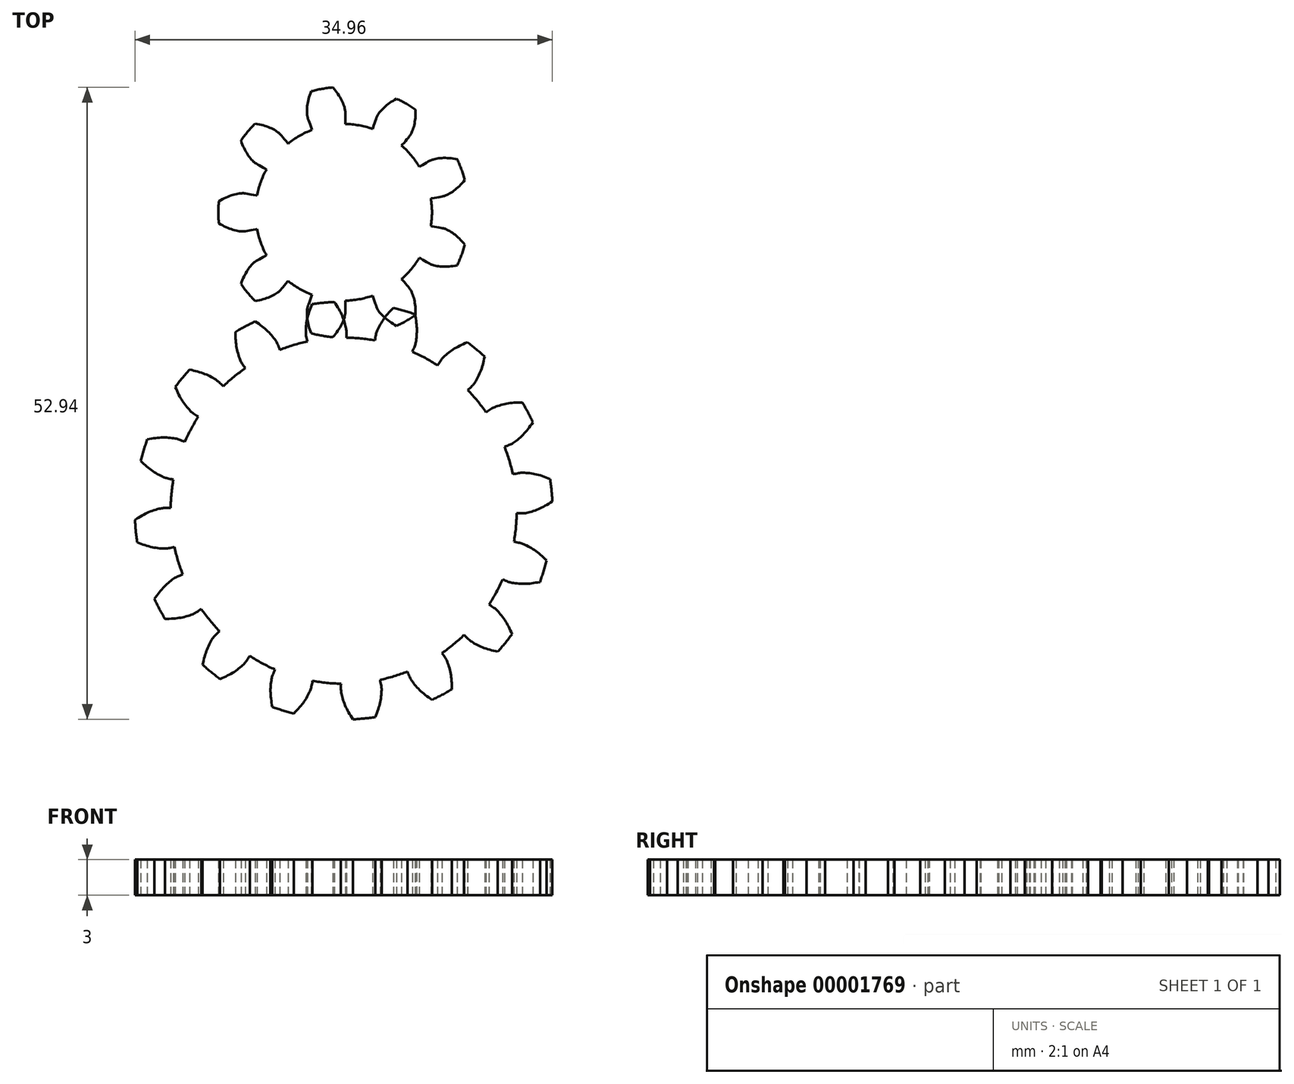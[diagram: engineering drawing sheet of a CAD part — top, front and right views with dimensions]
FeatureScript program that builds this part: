
annotation { "Feature Type Name" : "Feature", "Feature Type Description" : "" }
export const myFeature = defineFeature(function(context is Context, id is Id, definition is map)
    precondition{}
    {
        {
            var Q0;
            Q0=qCreatedBy(makeId("Top.planeOp"),FACE);
            var sketch = newSketch(context, id + "F0", { "sketchPlane" : qUnion([Q0])});
            skCircle(sketch, "E0", {"center": v(0, 0) * mm, "radius": 16 * mm});
            skLineSegment(sketch, "E1", {"start": v(0, 0) * mm, "end": v(0, 25) * mm, "construction": true});
            skLineSegment(sketch, "E2", {"start": v(0, 16) * mm, "end": v(15.76, 16) * mm, "construction": true});
            skLineSegment(sketch, "E3", {"start": v(-5.14, 14.13) * mm, "end": v(0, 16) * mm, "construction": true});
            skCircle(sketch, "E4", {"center": v(0, 0) * mm, "radius": 15.04 * mm});
            skArc(sketch, "E5", {"start": v(0.22, 15.03) * mm, "mid": v(-2.5, 14.83) * mm, "end": v(-5.14, 14.13) * mm, "construction": true});
            skArc(sketch, "E6", {"start": v(-5.14, 14.13) * mm, "mid": v(-6.07, 13.76) * mm, "end": v(-6.97, 13.32) * mm});
            skLineSegment(sketch, "E7", {"start": v(-6.97, 13.32) * mm, "end": v(-0.35, 16.79) * mm});
            skCircle(sketch, "E8", {"center": v(0, 25) * mm, "radius": 9 * mm});
            skCircle(sketch, "E9", {"center": v(0, 25) * mm, "radius": 8.46 * mm});
            skArc(sketch, "E10", {"start": v(-2.73, 14.78) * mm, "mid": v(-3.95, 14.5) * mm, "end": v(-5.14, 14.13) * mm});
            skLineSegment(sketch, "E11", {"start": v(-2.73, 14.78) * mm, "end": v(0.19, 15.32) * mm});
            skCircle(sketch, "E12", {"center": v(0, 0) * mm, "radius": 17.5 * mm});
            skLineSegment(sketch, "E13", {"start": v(0, 0) * mm, "end": v(-2.68, 27.22) * mm, "construction": true});
            skArc(sketch, "E14", {"start": v(-6.97, 13.32) * mm, "mid": v(-7.84, 12.83) * mm, "end": v(-8.68, 12.28) * mm});
            skLineSegment(sketch, "E15", {"start": v(-8.68, 12.28) * mm, "end": v(-0.94, 17.75) * mm});
            skLineSegment(sketch, "E16", {"start": v(0, 34) * mm, "end": v(7.65, 34) * mm, "construction": true});
            skLineSegment(sketch, "E17", {"start": v(0, 34) * mm, "end": v(-2.9, 32.95) * mm});
            skArc(sketch, "E18", {"start": v(0.13, 33.46) * mm, "mid": v(-1.4, 33.34) * mm, "end": v(-2.9, 32.95) * mm});
            skArc(sketch, "E19", {"start": v(-2.9, 32.95) * mm, "mid": v(-3.59, 32.66) * mm, "end": v(-4.25, 32.31) * mm});
            skArc(sketch, "E20", {"start": v(-4.25, 32.31) * mm, "mid": v(-4.88, 31.9) * mm, "end": v(-5.47, 31.45) * mm});
            skArc(sketch, "E21", {"start": v(-1.45, 33.33) * mm, "mid": v(-2.18, 33.17) * mm, "end": v(-2.9, 32.95) * mm});
            skLineSegment(sketch, "E22", {"start": v(-1.45, 33.33) * mm, "end": v(0.1, 33.6) * mm});
            skLineSegment(sketch, "E23", {"start": v(-4.25, 32.31) * mm, "end": v(-0.3, 34.61) * mm});
            skLineSegment(sketch, "E24", {"start": v(-5.47, 31.45) * mm, "end": v(-0.84, 35.38) * mm});
            skCircle(sketch, "E25", {"center": v(0, 25) * mm, "radius": 10.5 * mm});
            skCircle(sketch, "E26", {"center": v(0, 0) * mm, "radius": 14.5 * mm});
            skCircle(sketch, "E27", {"center": v(0, 25) * mm, "radius": 7.5 * mm});
            skLineSegment(sketch, "E28", {"start": v(0.22, 15.03) * mm, "end": v(0.22, 14.5) * mm});
            skLineSegment(sketch, "E29", {"start": v(0.13, 33.46) * mm, "end": v(0.13, 32.5) * mm});
            skArc(sketch, "E30", {"start": v(-5.47, 31.45) * mm, "mid": v(-6.02, 30.94) * mm, "end": v(-6.52, 30.38) * mm});
            skLineSegment(sketch, "E31", {"start": v(-6.52, 30.38) * mm, "end": v(-1.7, 36.23) * mm});
            skLineSegment(sketch, "E32", {"start": v(0, 40.35) * mm, "end": v(0, 25) * mm, "construction": true});
            skLineSegment(sketch, "E33", {"start": v(0, 25) * mm, "end": v(-3.05, 42.28) * mm, "construction": true});
            skSolve(sketch);
        }
        {
            var Q0;
            Q0=qCreatedBy(makeId("Top.planeOp"),FACE);
            var sketch = newSketch(context, id + "F1", { "sketchPlane" : qUnion([Q0])});
            skPoint(sketch, "E34.0", {"position": v(-1.7, 36.23) * mm});
            skLineSegment(sketch, "E34.1", {"start": v(0, 25) * mm, "end": v(-3.05, 42.28) * mm, "construction": true});
            skPoint(sketch, "E34.2", {"position": v(-0.84, 35.38) * mm});
            skPoint(sketch, "E34.3", {"position": v(-0.3, 34.61) * mm});
            skPoint(sketch, "E34.4", {"position": v(0, 34) * mm});
            skPoint(sketch, "E34.5", {"position": v(0.13, 33.46) * mm});
            skPoint(sketch, "E34.6", {"position": v(0.13, 32.5) * mm});
            skLineSegment(sketch, "E34.7", {"start": v(0, 40.35) * mm, "end": v(0, 25) * mm, "construction": true});
            skPoint(sketch, "E34.8", {"position": v(0.1, 33.6) * mm});
            skCircle(sketch, "E34.9", {"center": v(0, 25) * mm, "radius": 7.5 * mm, "construction": true});
            skFitSpline(sketch, "E35", {"points": [v(-1.7, 36.23) * mm, v(-0.84, 35.38) * mm, v(-0.3, 34.61) * mm, v(0, 34) * mm, v(0.1, 33.6) * mm, v(0.13, 33.46) * mm, v(0.13, 32.5) * mm], "startDerivative": vector(4.1, -3.72) * mm, "endDerivative": vector(-0.04, -5.95) * mm});
            skArc(sketch, "E36", {"start": v(-2.72, 35.14) * mm, "mid": v(1.82, 14.66) * mm, "end": v(-0.9, 35.46) * mm, "construction": true});
            skArc(sketch, "E37", {"start": v(-0.9, 35.46) * mm, "mid": v(-1.82, 35.34) * mm, "end": v(-2.72, 35.14) * mm});
            skCircle(sketch, "E38", {"center": v(0, 25) * mm, "radius": 7.4 * mm});
            skLineSegment(sketch, "E39", {"start": v(0.13, 32.5) * mm, "end": v(0.13, 32.4) * mm});
            skFitSpline(sketch, "E40.0.MirrorCS", {"points": [v(-2.24, 36.13) * mm, v(-2.76, 35.04) * mm, v(-3.01, 34.13) * mm, v(-3.08, 33.46) * mm, v(-3.05, 33.05) * mm, v(-3.01, 32.9) * mm, v(-2.68, 32) * mm], "startDerivative": vector(-2.57, -4.9) * mm, "endDerivative": vector(2.07, -5.58) * mm});
            skLineSegment(sketch, "E41.0.MirrorCS", {"start": v(-2.68, 32) * mm, "end": v(-2.65, 31.9) * mm});
            skSolve(sketch);
        }
        {
            var Q0;
            {var subQ2=sQuery(id+"F1.wireOp",EDGE,"E37");Q0=makeQuery(id+"F1.imprint","IMPRINT",FACE,{"disambiguationData":[TD([[makeQuery(id+"F1.imprint","IMPRINT",EDGE,{"derivedFrom":subQ2}),1.0]])]});}
            var Q1;
            {var subQ0=sQuery(id+"F1.wireOp",EDGE,"E38");var subQ2=makeQuery(id+"F1.imprint","INTERSECT",VERTEX,{"derivedFrom":[subQ0,sQuery(id+"F1.wireOp",EDGE,"E39")]});Q1=makeQuery(id+"F1.imprint","IMPRINT",FACE,{"disambiguationData":[TD([[makeQuery(id+"F1.imprint","IMPRINT",EDGE,{"disambiguationData":[TD([[subQ2,-1.0]])],"derivedFrom":subQ0}),1.0]])]});}
            var Q2;
            Q2=sQuery(id+"F1.wireOp",EDGE,"bd8be4a6-01c8-4a0f-9de7-5f540e58cdd51");
            extrude(context, id + "F2", {"entities" : qUnion([Q0, Q1]), "surfaceEntities" : qUnion([Q2]), "depth" : 3 * mm});
        }
        {
            var Q0;
            Q0=makeQuery(id+"F2.opExtrude","SWEPT_FACE",FACE,{"disambiguationData":[OSD([sQuery(id+"F1.wireOp",EDGE,"E35")])]});
            var Q1;
            Q1=makeQuery(id+"F2.opExtrude","SWEPT_FACE",FACE,{"disambiguationData":[OSD([sQuery(id+"F1.wireOp",EDGE,"E37")])]});
            var Q2;
            Q2=makeQuery(id+"F2.opExtrude","SWEPT_FACE",FACE,{"disambiguationData":[OSD([sQuery(id+"F1.wireOp",EDGE,"E40.0.MirrorCS")])]});
            var Q3;
            Q3=makeQuery(id+"F2.opExtrude","SWEPT_FACE",FACE,{"disambiguationData":[OSD([sQuery(id+"F1.wireOp",EDGE,"E41.0.MirrorCS")])]});
            var Q4;
            Q4=makeQuery(id+"F2.opExtrude","SWEPT_FACE",FACE,{"disambiguationData":[OSD([sQuery(id+"F1.wireOp",EDGE,"E39")])]});
            var Q5;
            Q5=makeQuery(id+"F2.opExtrude","SWEPT_BODY",BODY,{"disambiguationData":[OSD([sQuery(id+"F1.wireOp",EDGE,"64fa1176-3160-4ef3-af6c-22bc26c88087"),sQuery(id+"F1.wireOp",EDGE,"459d7c95-c125-41f0-bd05-e49a84881d8a"),sQuery(id+"F1.wireOp",EDGE,"60de48d5-e124-4f4f-a481-3a9ac85cb04c"),sQuery(id+"F1.wireOp",EDGE,"07be0122-f98c-4f97-823a-7fbccfa74c93.0.MirrorCS"),sQuery(id+"F1.wireOp",EDGE,"a7a360ef-c158-4e67-928c-88fdbf735fc3.0.MirrorCS"),sQuery(id+"F1.wireOp",EDGE,"bd8be4a6-01c8-4a0f-9de7-5f540e58cdd52")])]});
            var Q6;
            Q6=makeQuery(id+"F2.opExtrude","SWEPT_FACE",FACE,{"disambiguationData":[OSD([sQuery(id+"F1.wireOp",EDGE,"E38")])]});
            circularPattern(context, id + "F3", {"faces" : qUnion([Q0, Q1, Q2, Q3, Q4]), "axis" : qUnion([Q6]), "angle" : 360 * degree, "instanceCount" : 9, "equalSpace" : true, "patternType" : PatternType.FACE});
        }
        {
            var Q0;
            Q0=qCreatedBy(makeId("Top.planeOp"),FACE);
            var sketch = newSketch(context, id + "F4", { "sketchPlane" : qUnion([Q0])});
            skPoint(sketch, "E42.0", {"position": v(-0.94, 17.75) * mm});
            skPoint(sketch, "E42.1", {"position": v(-0.35, 16.79) * mm});
            skPoint(sketch, "E42.2", {"position": v(0, 16) * mm});
            skPoint(sketch, "E42.3", {"position": v(0.19, 15.32) * mm});
            skPoint(sketch, "E42.4", {"position": v(0.22, 15.03) * mm});
            skPoint(sketch, "E42.5", {"position": v(0.22, 14.5) * mm});
            skLineSegment(sketch, "E42.6", {"start": v(0, 0) * mm, "end": v(0, 25) * mm, "construction": true});
            skLineSegment(sketch, "E42.7", {"start": v(0, 0) * mm, "end": v(-2.68, 27.22) * mm, "construction": true});
            skCircle(sketch, "E42.8", {"center": v(0, 0) * mm, "radius": 14.5 * mm});
            skFitSpline(sketch, "E43", {"points": [v(-0.94, 17.75) * mm, v(-0.35, 16.79) * mm, v(0, 16) * mm, v(0.19, 15.32) * mm, v(0.22, 15.03) * mm, v(0.22, 14.5) * mm], "startDerivative": vector(2.45, -3.8) * mm, "endDerivative": vector(-0.04, -3.3) * mm});
            skFitSpline(sketch, "E44.0.MirrorCS", {"points": [v(-2.54, 17.59) * mm, v(-2.93, 16.53) * mm, v(-3.12, 15.7) * mm, v(-3.18, 15) * mm, v(-3.15, 14.7) * mm, v(-3.05, 14.18) * mm], "startDerivative": vector(-1.67, -4.2) * mm, "endDerivative": vector(0.69, -3.23) * mm});
            skArc(sketch, "E45", {"start": v(-2.65, 17.3) * mm, "mid": v(1.72, -17.42) * mm, "end": v(-0.77, 17.48) * mm, "construction": true});
            skArc(sketch, "E46", {"start": v(-0.77, 17.48) * mm, "mid": v(-1.72, 17.42) * mm, "end": v(-2.65, 17.3) * mm});
            skSolve(sketch);
        }
        {
            var Q0;
            {var subQ0=sQuery(id+"F4.wireOp",EDGE,"E42.8");var subQ2=makeQuery(id+"F4.imprint","INTERSECT",VERTEX,{"derivedFrom":[subQ0,sQuery(id+"F4.wireOp",EDGE,"E43")]});Q0=makeQuery(id+"F4.imprint","IMPRINT",FACE,{"disambiguationData":[TD([[makeQuery(id+"F4.imprint","IMPRINT",EDGE,{"disambiguationData":[TD([[subQ2,-1.0]])],"derivedFrom":subQ0}),1.0]])]});}
            var Q1;
            {var subQ0=sQuery(id+"F4.wireOp",EDGE,"E46");Q1=makeQuery(id+"F4.imprint","IMPRINT",FACE,{"disambiguationData":[TD([[makeQuery(id+"F4.imprint","IMPRINT",EDGE,{"derivedFrom":subQ0}),1.0]])]});}
            extrude(context, id + "F5", {"entities" : qUnion([Q0, Q1]), "depth" : 3 * mm});
        }
        {
            var Q0;
            Q0=makeQuery(id+"F5.opExtrude","SWEPT_FACE",FACE,{"disambiguationData":[OSD([sQuery(id+"F4.wireOp",EDGE,"E43")])]});
            var Q1;
            Q1=makeQuery(id+"F5.opExtrude","SWEPT_FACE",FACE,{"disambiguationData":[OSD([sQuery(id+"F4.wireOp",EDGE,"E46")])]});
            var Q2;
            Q2=makeQuery(id+"F5.opExtrude","SWEPT_FACE",FACE,{"disambiguationData":[OSD([sQuery(id+"F4.wireOp",EDGE,"E44.0.MirrorCS")])]});
            var Q3;
            Q3=makeQuery(id+"F5.opExtrude","SWEPT_FACE",FACE,{"disambiguationData":[OSD([sQuery(id+"F4.wireOp",EDGE,"E42.8")])]});
            circularPattern(context, id + "F6", {"faces" : qUnion([Q0, Q1, Q2]), "axis" : qUnion([Q3]), "angle" : 360 * degree, "instanceCount" : 16, "equalSpace" : true, "patternType" : PatternType.FACE});
        }
    });
